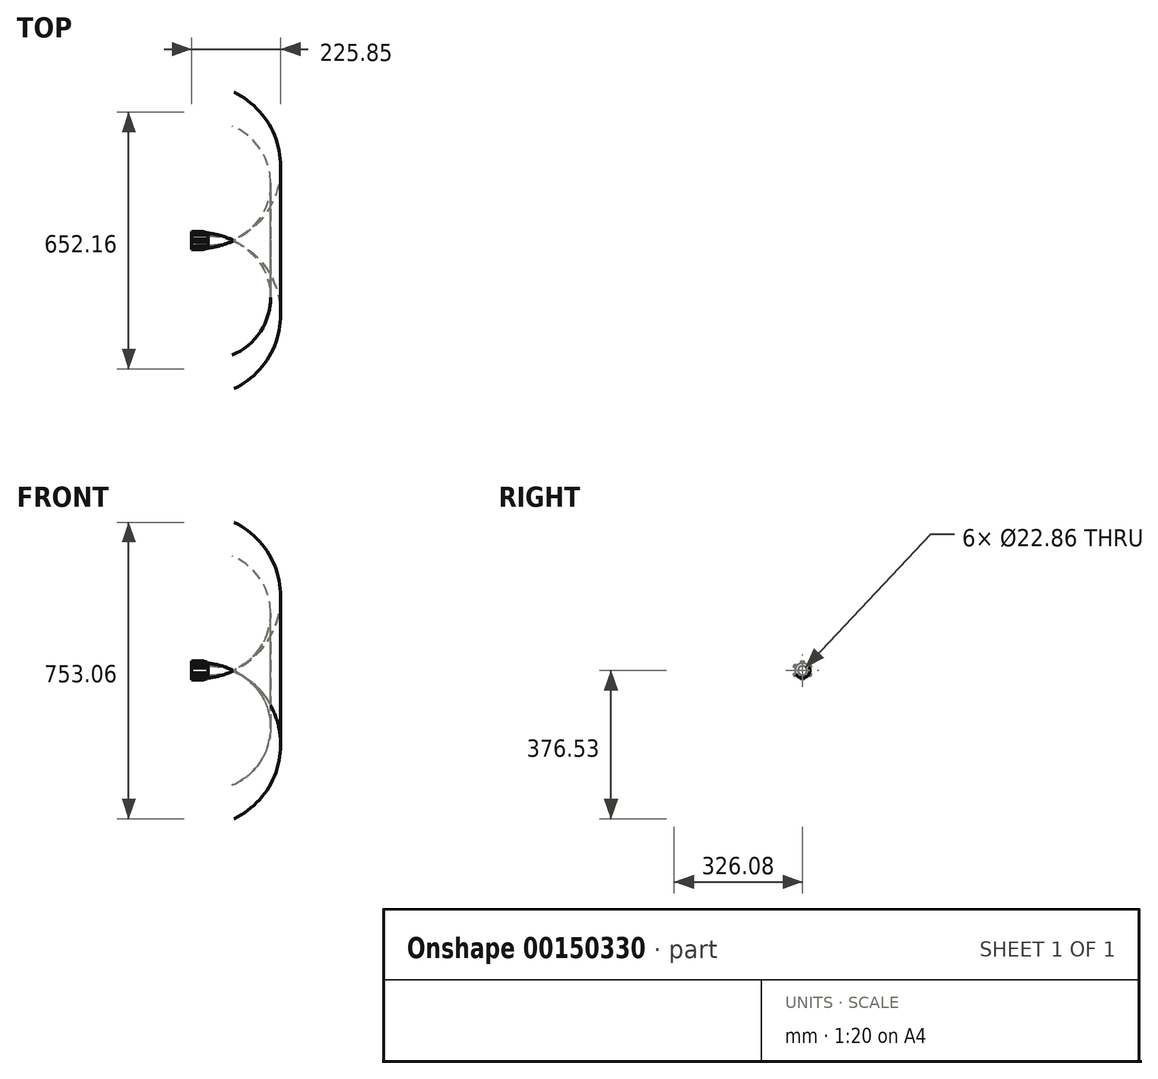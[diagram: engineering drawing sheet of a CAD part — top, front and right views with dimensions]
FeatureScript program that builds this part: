
annotation { "Feature Type Name" : "Feature", "Feature Type Description" : "" }
export const myFeature = defineFeature(function(context is Context, id is Id, definition is map)
    precondition{}
    {
        {
            var Q0;
            Q0=qCreatedBy(makeId("Front.planeOp"),FACE);
            var sketch = newSketch(context, id + "F0", { "sketchPlane" : qUnion([Q0])});
            skArc(sketch, "E0", {"start": v(61.1, 0) * mm, "mid": v(31.13, 8.77) * mm, "end": v(0, 11.43) * mm});
            skLineSegment(sketch, "E1", {"start": v(0, 11.43) * mm, "end": v(0, 18.9) * mm});
            skArc(sketch, "E2", {"start": v(65.87, 0) * mm, "mid": v(33.72, 12.17) * mm, "end": v(0, 18.9) * mm});
            skLineSegment(sketch, "E3", {"start": v(61.1, 0) * mm, "end": v(65.87, 0) * mm});
            skLineSegment(sketch, "E4", {"start": v(0, 0) * mm, "end": v(46.77, 0) * mm, "construction": true});
            skLineSegment(sketch, "E5", {"start": v(0, 11.43) * mm, "end": v(-41.12, 11.43) * mm});
            skLineSegment(sketch, "E6", {"start": v(-41.12, 11.43) * mm, "end": v(-41.12, 18.9) * mm});
            skLineSegment(sketch, "E7", {"start": v(-41.12, 18.9) * mm, "end": v(0, 18.9) * mm});
            skSolve(sketch);
        }
        {
            var Q0;
            Q0 = qSketchRegion(id + "F0", true);
            var Q1;
            Q1=sQuery(id+"F0.wireOp",EDGE,"E4");
            revolve(context, id + "F1", {"entities" : qUnion([Q0]), "axis" : qUnion([Q1]), "revolveType" : RevolveType.FULL});
        }
        {
            var Q0;
            Q0=makeQuery(id+"F1.opRevolve","SWEPT_FACE",FACE,{"disambiguationData":[OSD([sQuery(id+"F0.wireOp",EDGE,"E6")])]});
            var sketch = newSketch(context, id + "F2", { "sketchPlane" : qUnion([Q0])});
            skLineSegment(sketch, "E8.bottom", {"start": v(3.5, 24.15) * mm, "end": v(-3.5, 24.15) * mm});
            skLineSegment(sketch, "E8.top", {"start": v(3.5, 13.65) * mm, "end": v(-3.5, 13.65) * mm});
            skLineSegment(sketch, "E8.left", {"start": v(3.5, 24.15) * mm, "end": v(3.5, 13.65) * mm});
            skLineSegment(sketch, "E8.right", {"start": v(-3.5, 24.15) * mm, "end": v(-3.5, 13.65) * mm});
            skPoint(sketch, "E8.middle", {"position": v(0, 18.9) * mm});
            skSolve(sketch);
        }
        {
            var Q0;
            Q0 = qSketchRegion(id + "F2", true);
            extrude(context, id + "F3", {"entities" : qUnion([Q0]), "operationType" : NewBodyOperationType.ADD, "oppositeDirection" : true, "depth" : 37.46 * mm});
        }
        {
            var Q0;
            Q0=qCreatedBy(makeId("Front.planeOp"),FACE);
            var sketch = newSketch(context, id + "F4", { "sketchPlane" : qUnion([Q0])});
            skLineSegment(sketch, "E9", {"start": v(-21.32, 26.31) * mm, "end": v(4.86, 19.56) * mm});
            skLineSegment(sketch, "E10", {"start": v(4.86, 19.56) * mm, "end": v(4.86, 31.98) * mm});
            skLineSegment(sketch, "E11", {"start": v(4.86, 31.98) * mm, "end": v(-21.32, 26.31) * mm});
            skSolve(sketch);
        }
        {
            var Q0;
            Q0 = qSketchRegion(id + "F4", true);
            extrude(context, id + "F5", {"entities" : qUnion([Q0]), "operationType" : NewBodyOperationType.REMOVE, "endBound" : BoundingType.SYMMETRIC, "oppositeDirection" : true, "depth" : 25.4 * mm});
        }
        {
            var Q0;
            Q0=makeQuery(id+"F1.opRevolve","SWEPT_BODY",BODY,{"disambiguationData":[OSD([sQuery(id+"F0.wireOp",EDGE,"E0"),sQuery(id+"F0.wireOp",EDGE,"E2"),sQuery(id+"F0.wireOp",EDGE,"E3"),sQuery(id+"F0.wireOp",EDGE,"E5"),sQuery(id+"F0.wireOp",EDGE,"E6"),sQuery(id+"F0.wireOp",EDGE,"E7")])]});
            var Q1;
            Q1=makeQuery(id+"F1.opRevolve","SWEPT_FACE",FACE,{"disambiguationData":[OSD([sQuery(id+"F0.wireOp",EDGE,"E7")])]});
            circularPattern(context, id + "F6", {"entities" : qUnion([Q0]), "axis" : qUnion([Q1]), "angle" : 60 * degree, "instanceCount" : 6});
        }
    });
